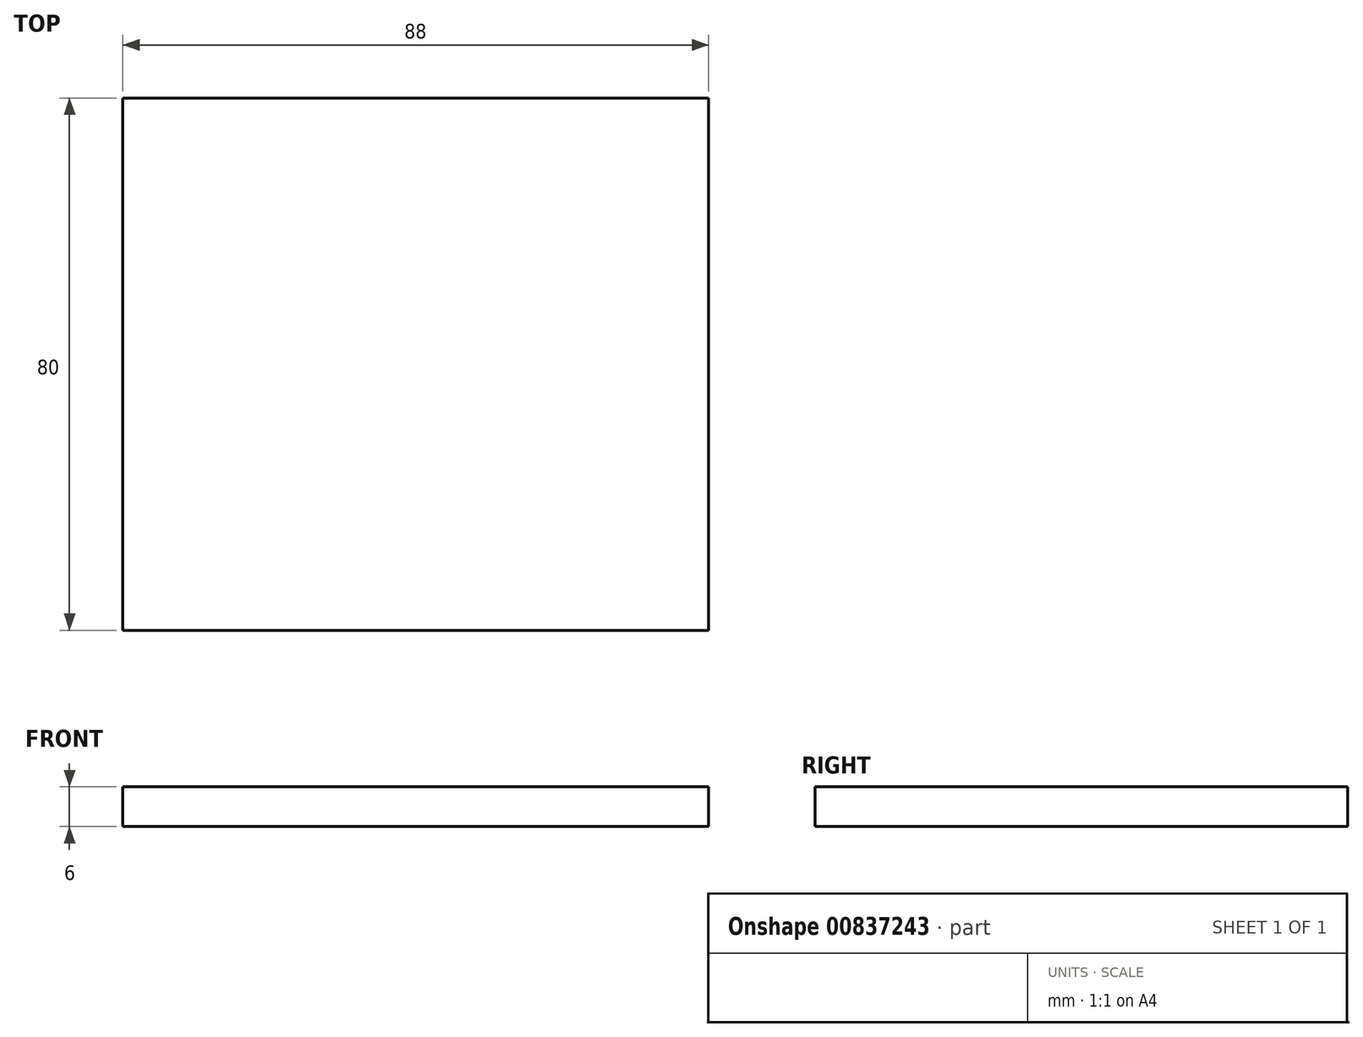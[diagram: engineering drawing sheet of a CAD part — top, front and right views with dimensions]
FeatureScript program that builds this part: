
annotation { "Feature Type Name" : "Feature", "Feature Type Description" : "" }
export const myFeature = defineFeature(function(context is Context, id is Id, definition is map)
    precondition{}
    {
        {
            var Q0;
            Q0=qCreatedBy(makeId("Top.planeOp"),FACE);
            var sketch = newSketch(context, id + "F0", { "sketchPlane" : qUnion([Q0])});
            skLineSegment(sketch, "E0.bottom", {"start": v(44, -40) * mm, "end": v(-44, -40) * mm});
            skLineSegment(sketch, "E0.top", {"start": v(44, 40) * mm, "end": v(-44, 40) * mm});
            skLineSegment(sketch, "E0.left", {"start": v(44, -40) * mm, "end": v(44, 40) * mm});
            skLineSegment(sketch, "E0.right", {"start": v(-44, -40) * mm, "end": v(-44, 40) * mm});
            skPoint(sketch, "E0.middle", {"position": v(0, 0) * mm});
            skSolve(sketch);
        }
        {
            var Q0;
            Q0 = qSketchRegion(id + "F0", true);
            extrude(context, id + "F1", {"entities" : qUnion([Q0]), "depth" : 6 * mm, "offsetDistance" : 25.4 * mm});
        }
    });
